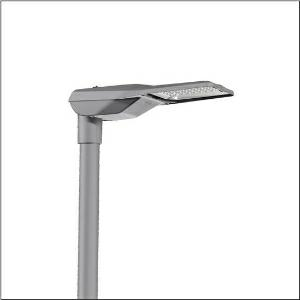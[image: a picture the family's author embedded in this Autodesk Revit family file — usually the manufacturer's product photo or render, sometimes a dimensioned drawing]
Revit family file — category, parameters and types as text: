
# Revit family: streetlight_sl_21_iq_mini___p0_8ab_5xe2r31v08jb_ae49
name_source: partatom
category: Lighting Fixtures
units: mm (PartAtom-declared; Revit-internal decimal feet)

## family parameters
Cut with Voids When Loaded = No
Host = Face
Light Source = No
Part Type = Normal
Room Calculation Point = No
Round Connector Dimension = Use Diameter
Shared = No

## types (1)
- --- (1 x LED, 9740 lm, 72.5 W, 3000K)
    Apparent Load = 73 VA
    CIE Flux Codes = 39 72 97 100 100
    Color Rendering = 70
    Color Temperature = 3000K
    Default Elevation = 1800 mm
    Description = Streetlight SL 21 iQ mini, mast luminaire, primary light control with lens, of PMMA, primary optical cover: cover, of toughened safety glass, transparent, light distribution: P0.8aB, light emission: direct distribution, primary light characteristic: asymmetric, installation type: post-top, side-entry, LED, High Power LED, rated luminous flux: 9.740lm, luminous efficacy: 134lm/W, light colour: 730, colour temperature: 3000K, control gear: iQ-Street Remote, D4i with power reduction, control: pre-setting: logarithmic dimming characteristic, Street-Remote, Auto-Match, Temp-Guard, Lumen-Switch, Night-Set, Smart-Wire, Light-Fading, Desk-Remote (wireless, voltage-free reading and setting of iQ features in the workshop via application-optimized NFC function/RFID function), optimised constant luminous flux control (CLO 2.0), mains connection: 220..240V, AC, 50/60Hz, start of lifetime: 73W, end of service life: 76W, reduction: 33W, luminaire housing, of diecast aluminium, powder-coated, Siteco® metallic grey (DB 702S), corrosivity category C5 mid according to DIN EN ISO 12944, please order mast flange separately, inclination adjustable: 0°, 5°, 10°, 15°, sealing non-destructively replaceable, multi-level sealing system, length: 628mm, width: 235mm, height: 110mm, mast flange for spigot size: 42mm (side-entry): 5XC10008XM4, 60/48mm (side-entry/post-top): 5XC10108XM2, 76/60mm (side-entry/post-top): 5XC10108XM1, mounting height: 4..8m, Smart Interface above, protection rating (complete): IP66, insulation class (complete): insulation class II (safety insulation), certification: CE, ENEC, ENEC+, VDE, impact resistance: IK10, permissible operating ambient temperature for outdoor applications: -40..+50°C, standard-compliant lighting for roads and squares, packaging unit: 1 piece

Light Distribution: P0.8aB
    Height = 110 mm
    Lamp = 1 x LED
    Lamp Light Flux = 9740 lm
    Lamp Power = 72.5 W
    Lamp count = 1
    Length = 625 mm
    Luminous efficacy = 134 lm/W
    Manufacturer = Siteco
    ModVariant = No
    Model = 5XE2R31V08JB
    Number of Poles = 1
    OnlyDefault = Yes
    Power Factor = 1
    Product Name = Streetlight SL 21 iQ mini | P0.8aB
    Product group = mast luminaire | pylon top
    ProductGroupID = 6100
    Protection Class = Protection class II
    Protection Degree = IP 66
    RLX_Detail_Level = 1
    RLX_Emergency_Light_Flux = 0 lm
    RLX_Emergency_Type = 0
    RLX_Emergency_Type_DB = No
    RlxData = <blob elided: 26097 chars, md5=84098e19>
    Socket = socket
    Standby Power = 0 W
    System Light Flux = 9740 lm
    System Power = 73 W
    Type Comments = factory setting: luminous flux: 100 % | dim-lin: 254 | 755 mA
    Type Image = l_1003515.jpg
    URL = http://relux.com
    VarID = @adj_071326
    Voltage = 0 V
    Weight = 0.00 kg
    Width = 234 mm

## geometry (parser evidence)
native form markers: Blend x4, Sweep x9
no freeform markers — native parametric forms only
